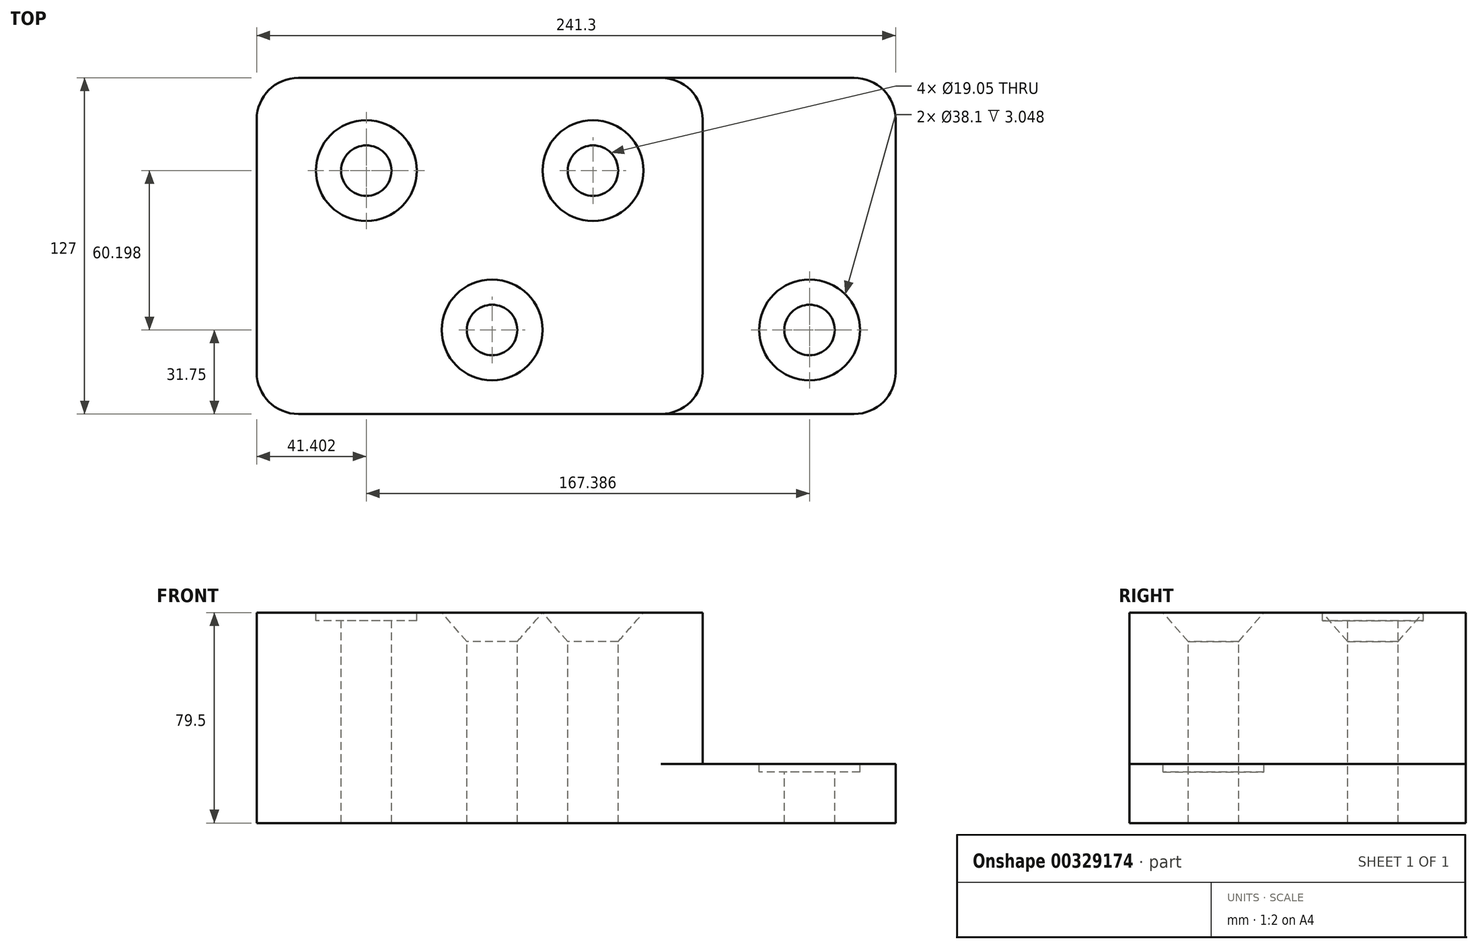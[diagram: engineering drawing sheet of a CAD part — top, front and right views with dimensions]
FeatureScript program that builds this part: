
annotation { "Feature Type Name" : "Feature", "Feature Type Description" : "" }
export const myFeature = defineFeature(function(context is Context, id is Id, definition is map)
    precondition{}
    {
        {
            var Q0;
            Q0=qCreatedBy(makeId("Front.planeOp"),FACE);
            var sketch = newSketch(context, id + "F0", { "sketchPlane" : qUnion([Q0])});
            skLineSegment(sketch, "E0", {"start": v(0, 0) * mm, "end": v(0, 79.5) * mm});
            skLineSegment(sketch, "E1", {"start": v(0, 79.5) * mm, "end": v(168.4, 79.5) * mm});
            skLineSegment(sketch, "E2", {"start": v(168.4, 79.5) * mm, "end": v(168.4, 22.35) * mm});
            skLineSegment(sketch, "E3", {"start": v(168.4, 22.35) * mm, "end": v(241.3, 22.35) * mm});
            skLineSegment(sketch, "E4", {"start": v(241.3, 22.35) * mm, "end": v(241.3, 0) * mm});
            skLineSegment(sketch, "E5", {"start": v(241.3, 0) * mm, "end": v(0, 0) * mm});
            skSolve(sketch);
        }
        {
            var Q0;
            Q0=makeQuery(id+"F0.imprint","IMPRINT",FACE,{"disambiguationData":[TD([[makeQuery(id+"F0.imprint","IMPRINT",EDGE,{"derivedFrom":sQuery(id+"F0.wireOp",EDGE,"E0")}),-1.0]])]});
            extrude(context, id + "F1", {"entities" : qUnion([Q0]), "depth" : 127 * mm});
        }
        {
            var Q0;
            Q0=makeQuery(id+"F1.opExtrude","CAP_EDGE",EDGE,{"disambiguationData":[OSD([sQuery(id+"F0.wireOp",EDGE,"E0")])],"isStart":false});
            var Q1;
            Q1=makeQuery(id+"F1.opExtrude","CAP_EDGE",EDGE,{"disambiguationData":[OSD([sQuery(id+"F0.wireOp",EDGE,"E2")])],"isStart":false});
            var Q2;
            Q2=makeQuery(id+"F1.opExtrude","CAP_EDGE",EDGE,{"disambiguationData":[OSD([sQuery(id+"F0.wireOp",EDGE,"E2")])],"isStart":true});
            var Q3;
            Q3=makeQuery(id+"F1.opExtrude","CAP_EDGE",EDGE,{"disambiguationData":[OSD([sQuery(id+"F0.wireOp",EDGE,"E4")])],"isStart":true});
            var Q4;
            Q4=makeQuery(id+"F1.opExtrude","CAP_EDGE",EDGE,{"disambiguationData":[OSD([sQuery(id+"F0.wireOp",EDGE,"E4")])],"isStart":false});
            var Q5;
            Q5=makeQuery(id+"F1.opExtrude","CAP_EDGE",EDGE,{"disambiguationData":[OSD([sQuery(id+"F0.wireOp",EDGE,"E0")])],"isStart":true});
            fillet(context, id + "F2", {"entities" : qUnion([Q0, Q1, Q2, Q3, Q4, Q5]), "radius" : 15.75 * mm, "tangentPropagation" : true, "allowEdgeOverflow" : false});
        }
        {
            var Q0;
            Q0=makeQuery(id+"F1.opExtrude","SWEPT_FACE",FACE,{"disambiguationData":[OSD([sQuery(id+"F0.wireOp",EDGE,"E1")])]});
            var sketch = newSketch(context, id + "F3", { "sketchPlane" : qUnion([Q0])});
            skCircle(sketch, "E6", {"center": v(41.4, -35.05) * mm, "radius": 9.53 * mm});
            skCircle(sketch, "E7", {"center": v(88.9, -95.25) * mm, "radius": 9.53 * mm});
            skCircle(sketch, "E8", {"center": v(127, -35.05) * mm, "radius": 9.53 * mm});
            skCircle(sketch, "E9", {"center": v(41.4, -35.05) * mm, "radius": 19.05 * mm});
            skCircle(sketch, "E10", {"center": v(127, -35.05) * mm, "radius": 19.05 * mm});
            skCircle(sketch, "E11", {"center": v(88.9, -95.25) * mm, "radius": 19.05 * mm});
            skSolve(sketch);
        }
        {
            var Q0;
            Q0=sQuery(id+"F3.wireOp",VERTEX,"E7.center");
            var Q1;
            Q1=makeQuery(id+"F1.opExtrude","SWEPT_BODY",BODY,{"disambiguationData":[OSD([sQuery(id+"F0.wireOp",EDGE,"E0"),sQuery(id+"F0.wireOp",EDGE,"E1"),sQuery(id+"F0.wireOp",EDGE,"E2"),sQuery(id+"F0.wireOp",EDGE,"E3"),sQuery(id+"F0.wireOp",EDGE,"E4"),sQuery(id+"F0.wireOp",EDGE,"E5")])]});
            hole(context, id + "F4", {"style" : HoleStyle.C_SINK, "endStyle" : HoleEndStyle.THROUGH, "holeDiameter" : 19.05 * mm, "cSinkDiameter" : 38.1 * mm, "cSinkAngle" : 82 * degree, "tappedDepth" : 12.7 * mm, "tapClearance" : 3, "startFromSketch" : true, "locations" : qUnion([Q0]), "scope" : qUnion([Q1])});
        }
        {
            var Q0;
            Q0=sQuery(id+"F3.wireOp",VERTEX,"E6.center");
            var Q1;
            Q1=makeQuery(id+"F1.opExtrude","SWEPT_BODY",BODY,{"disambiguationData":[OSD([sQuery(id+"F0.wireOp",EDGE,"E0"),sQuery(id+"F0.wireOp",EDGE,"E1"),sQuery(id+"F0.wireOp",EDGE,"E2"),sQuery(id+"F0.wireOp",EDGE,"E3"),sQuery(id+"F0.wireOp",EDGE,"E4"),sQuery(id+"F0.wireOp",EDGE,"E5")])]});
            hole(context, id + "F5", {"style" : HoleStyle.C_BORE, "endStyle" : HoleEndStyle.THROUGH, "holeDiameter" : 19.05 * mm, "cBoreDiameter" : 38.1 * mm, "cBoreDepth" : 3.05 * mm, "tappedDepth" : 12.7 * mm, "tapClearance" : 3, "startFromSketch" : true, "locations" : qUnion([Q0]), "scope" : qUnion([Q1])});
        }
        {
            var Q0;
            Q0=makeQuery(id+"F1.opExtrude","SWEPT_FACE",FACE,{"disambiguationData":[OSD([sQuery(id+"F0.wireOp",EDGE,"E3")])]});
            var sketch = newSketch(context, id + "F6", { "sketchPlane" : qUnion([Q0])});
            skCircle(sketch, "E12", {"center": v(208.79, -95.25) * mm, "radius": 19.05 * mm});
            skSolve(sketch);
        }
        {
            var Q0;
            Q0=sQuery(id+"F6.wireOp",VERTEX,"E12.center");
            var Q1;
            Q1=makeQuery(id+"F1.opExtrude","SWEPT_BODY",BODY,{"disambiguationData":[OSD([sQuery(id+"F0.wireOp",EDGE,"E0"),sQuery(id+"F0.wireOp",EDGE,"E1"),sQuery(id+"F0.wireOp",EDGE,"E2"),sQuery(id+"F0.wireOp",EDGE,"E3"),sQuery(id+"F0.wireOp",EDGE,"E4"),sQuery(id+"F0.wireOp",EDGE,"E5")])]});
            hole(context, id + "F7", {"style" : HoleStyle.C_BORE, "endStyle" : HoleEndStyle.THROUGH, "holeDiameter" : 19.05 * mm, "cBoreDiameter" : 38.1 * mm, "cBoreDepth" : 3.05 * mm, "tappedDepth" : 12.7 * mm, "tapClearance" : 3, "startFromSketch" : true, "locations" : qUnion([Q0]), "scope" : qUnion([Q1])});
        }
        {
            var Q0;
            Q0=sQuery(id+"F3.wireOp",VERTEX,"E8.center");
            var Q1;
            Q1=makeQuery(id+"F1.opExtrude","SWEPT_BODY",BODY,{"disambiguationData":[OSD([sQuery(id+"F0.wireOp",EDGE,"E0"),sQuery(id+"F0.wireOp",EDGE,"E1"),sQuery(id+"F0.wireOp",EDGE,"E2"),sQuery(id+"F0.wireOp",EDGE,"E3"),sQuery(id+"F0.wireOp",EDGE,"E4"),sQuery(id+"F0.wireOp",EDGE,"E5")])]});
            hole(context, id + "F8", {"style" : HoleStyle.C_SINK, "endStyle" : HoleEndStyle.THROUGH, "holeDiameter" : 19.05 * mm, "cSinkDiameter" : 38.1 * mm, "cSinkAngle" : 82 * degree, "tappedDepth" : 12.7 * mm, "tapClearance" : 3, "startFromSketch" : true, "locations" : qUnion([Q0]), "scope" : qUnion([Q1])});
        }
    });
